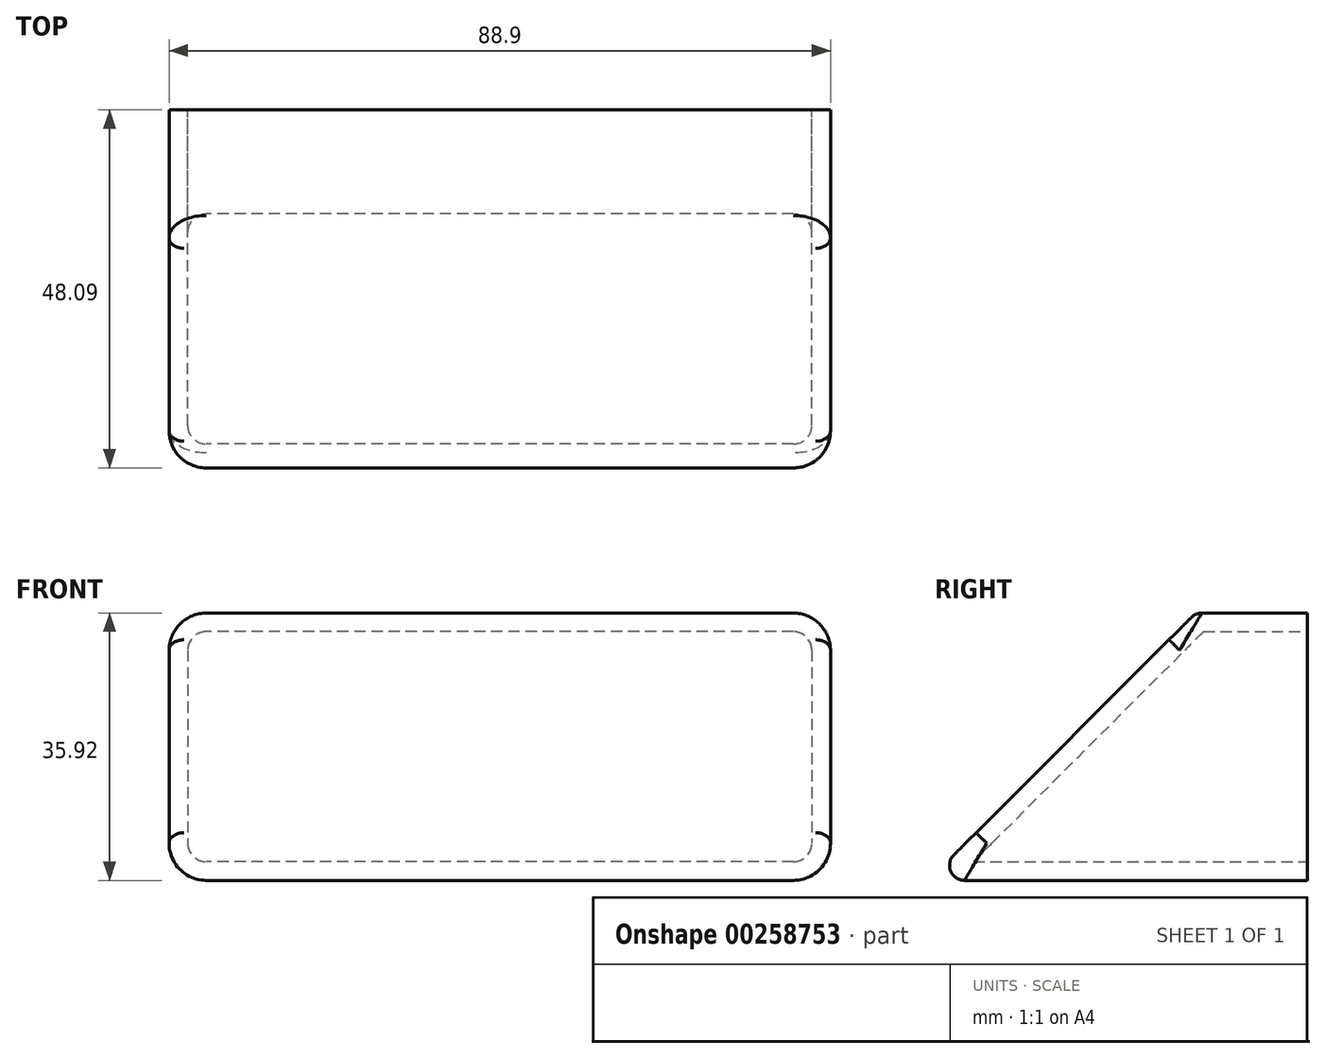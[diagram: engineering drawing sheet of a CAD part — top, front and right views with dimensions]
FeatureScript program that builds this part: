
annotation { "Feature Type Name" : "Feature", "Feature Type Description" : "" }
export const myFeature = defineFeature(function(context is Context, id is Id, definition is map)
    precondition{}
    {
        {
            assignVariable(context, id + "F0", {"name" : "w_card", "anyValue" : 88.9 * mm});
        }
        {
            assignVariable(context, id + "F1", {"name" : "t", "anyValue" : 2.5});
        }
        {
            assignVariable(context, id + "F2", {"name" : "fillet", "anyValue" : 5});
        }
        {
            var Q0;
            Q0=qCreatedBy(makeId("Right.planeOp"),FACE);
            var sketch = newSketch(context, id + "F3", { "sketchPlane" : qUnion([Q0])});
            skLineSegment(sketch, "E0", {"start": v(-35.92, 0) * mm, "end": v(0, 35.92) * mm});
            skLineSegment(sketch, "E1", {"start": v(0, 35.92) * mm, "end": v(15, 35.92) * mm});
            skLineSegment(sketch, "E2", {"start": v(15, 35.92) * mm, "end": v(15, 0) * mm});
            skLineSegment(sketch, "E3", {"start": v(15, 0) * mm, "end": v(-35.92, 0) * mm});
            skSolve(sketch);
        }
        {
            var Q0;
            Q0 = qSketchRegion(id + "F3", true);
            extrude(context, id + "F4", {"entities" : qUnion([Q0]), "endBound" : BoundingType.SYMMETRIC, "depth" : getVariable(context, 'w_card')});
        }
        {
            var Q0;
            Q0=makeQuery(id+"F4.opExtrude","CAP_EDGE",EDGE,{"disambiguationData":[OSD([sQuery(id+"F3.wireOp",EDGE,"E1")])],"isStart":false});
            var Q1;
            Q1=makeQuery(id+"F4.opExtrude","CAP_EDGE",EDGE,{"disambiguationData":[OSD([sQuery(id+"F3.wireOp",EDGE,"E3")])],"isStart":false});
            var Q2;
            Q2=makeQuery(id+"F4.opExtrude","CAP_EDGE",EDGE,{"disambiguationData":[OSD([sQuery(id+"F3.wireOp",EDGE,"E1")])],"isStart":true});
            var Q3;
            Q3=makeQuery(id+"F4.opExtrude","CAP_EDGE",EDGE,{"disambiguationData":[OSD([sQuery(id+"F3.wireOp",EDGE,"E3")])],"isStart":true});
            fillet(context, id + "F5", {"entities" : qUnion([Q0, Q1, Q2, Q3]), "radius" : (getVariable(context, 'fillet')) * mm, "tangentPropagation" : true, "allowEdgeOverflow" : false});
        }
        {
            var Q0;
            Q0=makeQuery(id+"F4.opExtrude","SWEPT_FACE",FACE,{"disambiguationData":[OSD([sQuery(id+"F3.wireOp",EDGE,"E2")])]});
            shell(context, id + "F6", {"entities" : qUnion([Q0]), "thickness" : (getVariable(context, 't')) * mm});
        }
        {
            var Q0;
            Q0=makeQuery(id+"F4.opExtrude","SWEPT_EDGE",EDGE,{"disambiguationData":[OSD([sQuery(id+"F3.wireOp",EDGE,"E0"),sQuery(id+"F3.wireOp",EDGE,"E3")])]});
            fillet(context, id + "F7", {"entities" : qUnion([Q0]), "radius" : 2 * mm, "tangentPropagation" : true, "allowEdgeOverflow" : false});
        }
    });
